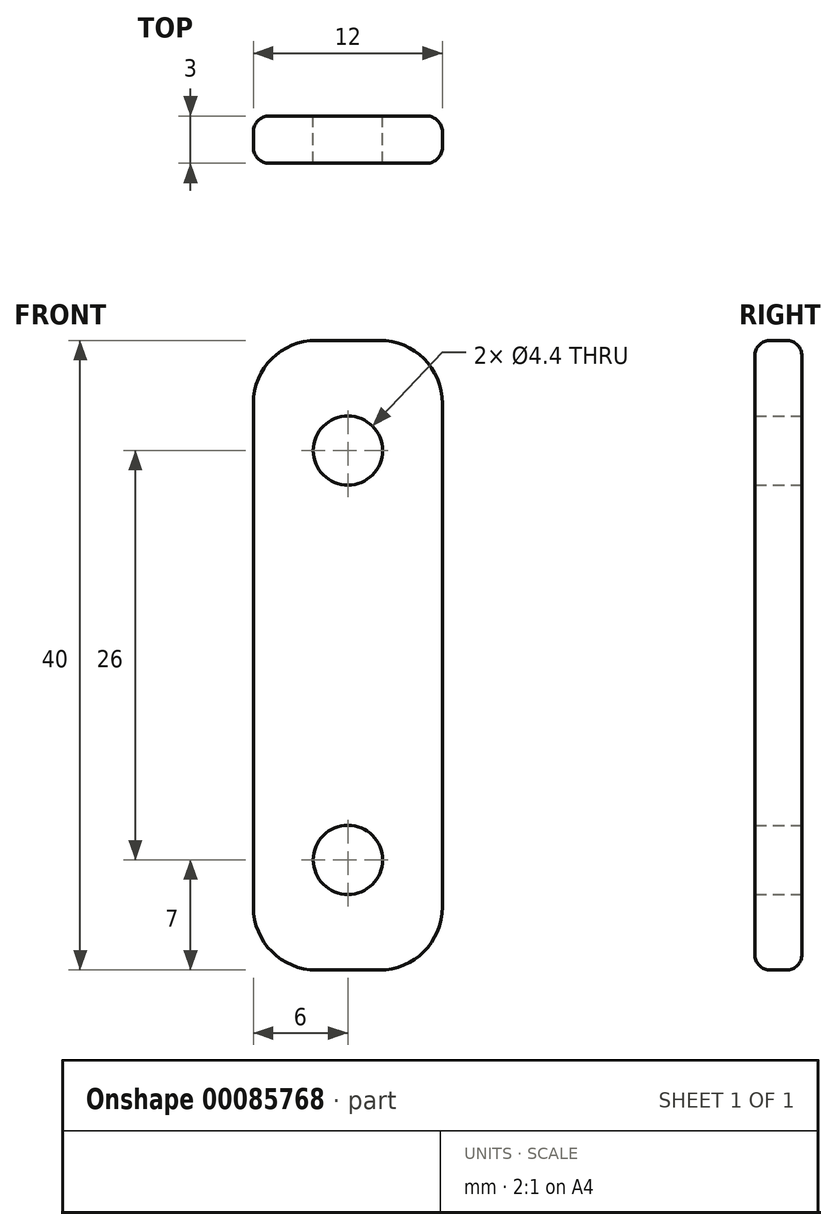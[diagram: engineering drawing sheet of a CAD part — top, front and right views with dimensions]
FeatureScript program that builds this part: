
annotation { "Feature Type Name" : "Feature", "Feature Type Description" : "" }
export const myFeature = defineFeature(function(context is Context, id is Id, definition is map)
    precondition{}
    {
        {
            var Q0;
            Q0=qCreatedBy(makeId("Front.planeOp"),FACE);
            var sketch = newSketch(context, id + "F0", { "sketchPlane" : qUnion([Q0])});
            skLineSegment(sketch, "E0.bottom", {"start": v(6, 20) * mm, "end": v(-6, 20) * mm});
            skLineSegment(sketch, "E0.top", {"start": v(6, -20) * mm, "end": v(-6, -20) * mm});
            skLineSegment(sketch, "E0.left", {"start": v(6, 20) * mm, "end": v(6, -20) * mm});
            skLineSegment(sketch, "E0.right", {"start": v(-6, 20) * mm, "end": v(-6, -20) * mm});
            skPoint(sketch, "E0.middle", {"position": v(0, 0) * mm});
            skSolve(sketch);
        }
        {
            var Q0;
            Q0=makeQuery(id+"F0.imprint","IMPRINT",FACE,{"disambiguationData":[TD([[makeQuery(id+"F0.imprint","IMPRINT",EDGE,{"derivedFrom":sQuery(id+"F0.wireOp",EDGE,"E0.bottom")}),1.0]])]});
            extrude(context, id + "F1", {"entities" : qUnion([Q0]), "depth" : 3 * mm});
        }
        {
            var Q0;
            Q0=makeQuery(id+"F1.opExtrude","SWEPT_EDGE",EDGE,{"disambiguationData":[OSD([sQuery(id+"F0.wireOp",EDGE,"E0.bottom"),sQuery(id+"F0.wireOp",EDGE,"E0.left")])]});
            var Q1;
            Q1=makeQuery(id+"F1.opExtrude","SWEPT_EDGE",EDGE,{"disambiguationData":[OSD([sQuery(id+"F0.wireOp",EDGE,"E0.bottom"),sQuery(id+"F0.wireOp",EDGE,"E0.right")])]});
            var Q2;
            Q2=makeQuery(id+"F1.opExtrude","SWEPT_EDGE",EDGE,{"disambiguationData":[OSD([sQuery(id+"F0.wireOp",EDGE,"E0.top"),sQuery(id+"F0.wireOp",EDGE,"E0.left")])]});
            var Q3;
            Q3=makeQuery(id+"F1.opExtrude","SWEPT_EDGE",EDGE,{"disambiguationData":[OSD([sQuery(id+"F0.wireOp",EDGE,"E0.top"),sQuery(id+"F0.wireOp",EDGE,"E0.right")])]});
            fillet(context, id + "F2", {"entities" : qUnion([Q0, Q1, Q2, Q3]), "radius" : 4 * mm, "tangentPropagation" : true, "allowEdgeOverflow" : false});
        }
        {
            var Q0;
            Q0=makeQuery(id+"F1.opExtrude","CAP_EDGE",EDGE,{"disambiguationData":[OSD([sQuery(id+"F0.wireOp",EDGE,"E0.left")])],"isStart":false});
            var Q1;
            Q1=makeQuery(id+"F1.opExtrude","CAP_EDGE",EDGE,{"disambiguationData":[OSD([sQuery(id+"F0.wireOp",EDGE,"E0.left")])],"isStart":true});
            var Q2;
            Q2=makeQuery(id+"F1.opExtrude","CAP_EDGE",EDGE,{"disambiguationData":[OSD([sQuery(id+"F0.wireOp",EDGE,"E0.right")])],"isStart":true});
            var Q3;
            Q3=makeQuery(id+"F1.opExtrude","CAP_EDGE",EDGE,{"disambiguationData":[OSD([sQuery(id+"F0.wireOp",EDGE,"E0.right")])],"isStart":false});
            fillet(context, id + "F3", {"entities" : qUnion([Q0, Q1, Q2, Q3]), "radius" : 1 * mm, "tangentPropagation" : true, "allowEdgeOverflow" : false});
        }
        {
            var Q0;
            Q0=qCreatedBy(makeId("Front.planeOp"),FACE);
            var sketch = newSketch(context, id + "F4", { "sketchPlane" : qUnion([Q0])});
            skPoint(sketch, "E1", {"position": v(0, 13) * mm});
            skPoint(sketch, "E2.MirrorP", {"position": v(0, -13) * mm});
            skSolve(sketch);
        }
        {
            var Q0;
            Q0=sQuery(id+"F4.wireOp",VERTEX,"E1");
            var Q1;
            Q1=sQuery(id+"F4.wireOp",VERTEX,"E2.MirrorP");
            var Q2;
            Q2=makeQuery(id+"F1.opExtrude","SWEPT_BODY",BODY,{"disambiguationData":[OSD([sQuery(id+"F0.wireOp",EDGE,"E0.bottom"),sQuery(id+"F0.wireOp",EDGE,"E0.top"),sQuery(id+"F0.wireOp",EDGE,"E0.left"),sQuery(id+"F0.wireOp",EDGE,"E0.right")])]});
            hole(context, id + "F5", {"style" : HoleStyle.C_BORE, "endStyle" : HoleEndStyle.BLIND, "oppositeDirection" : true, "holeDiameter" : 4.4 * mm, "cBoreDiameter" : 4.4 * mm, "cBoreDepth" : 4 * mm, "holeDepth" : 30 * mm, "locations" : qUnion([Q0, Q1]), "scope" : qUnion([Q2])});
        }
    });
